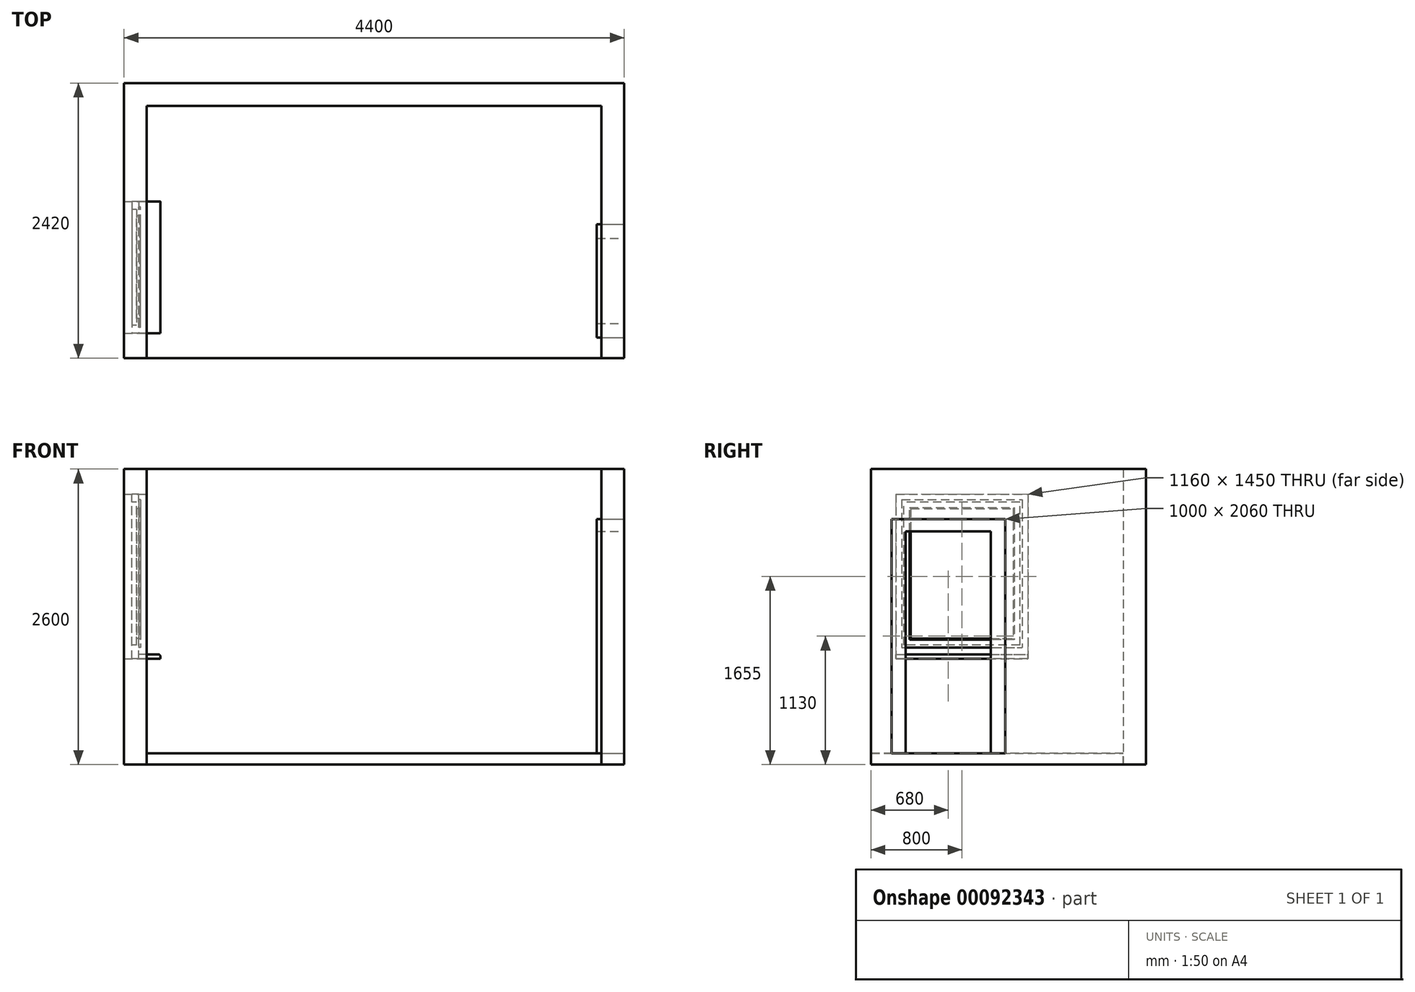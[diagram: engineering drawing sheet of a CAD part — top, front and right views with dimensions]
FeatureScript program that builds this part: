
annotation { "Feature Type Name" : "Feature", "Feature Type Description" : "" }
export const myFeature = defineFeature(function(context is Context, id is Id, definition is map)
    precondition{}
    {
        {
            var Q0;
            Q0=qCreatedBy(makeId("Top.planeOp"),FACE);
            var sketch = newSketch(context, id + "F0", { "sketchPlane" : qUnion([Q0])});
            skLineSegment(sketch, "E0", {"start": v(-2000, 1110) * mm, "end": v(2000, 1110) * mm});
            skLineSegment(sketch, "E1", {"start": v(2000, 1110) * mm, "end": v(2000, -1110) * mm});
            skLineSegment(sketch, "E2", {"start": v(2000, -1110) * mm, "end": v(-2000, -1110) * mm});
            skLineSegment(sketch, "E3", {"start": v(-2000, -1110) * mm, "end": v(-2000, 1110) * mm});
            skSolve(sketch);
        }
        {
            var Q0;
            Q0 = qSketchRegion(id + "F0", true);
            extrude(context, id + "F1", {"entities" : qUnion([Q0]), "oppositeDirection" : true, "depth" : 100 * mm});
        }
        {
            var Q0;
            Q0=makeQuery(id+"F1.opExtrude","CAP_FACE",FACE,{"disambiguationData":[OSD([sQuery(id+"F0.wireOp",EDGE,"E0"),sQuery(id+"F0.wireOp",EDGE,"E1"),sQuery(id+"F0.wireOp",EDGE,"E2"),sQuery(id+"F0.wireOp",EDGE,"E3")])],"isStart":true});
            var sketch = newSketch(context, id + "F2", { "sketchPlane" : qUnion([Q0])});
            skLineSegment(sketch, "E4", {"start": v(-2000, -1110) * mm, "end": v(-2000, 1110) * mm});
            skLineSegment(sketch, "E5", {"start": v(-2000, 1110) * mm, "end": v(2000, 1110) * mm});
            skLineSegment(sketch, "E6", {"start": v(2000, 1110) * mm, "end": v(2000, -1110) * mm});
            skLineSegment(sketch, "E7", {"start": v(2000, -1110) * mm, "end": v(2200, -1110) * mm});
            skLineSegment(sketch, "E8", {"start": v(2200, -1110) * mm, "end": v(2200, 1310) * mm});
            skLineSegment(sketch, "E9", {"start": v(2200, 1310) * mm, "end": v(-2200, 1310) * mm});
            skLineSegment(sketch, "E10", {"start": v(-2200, 1310) * mm, "end": v(-2200, -1110) * mm});
            skLineSegment(sketch, "E11", {"start": v(-2200, -1110) * mm, "end": v(-2000, -1110) * mm});
            skSolve(sketch);
        }
        {
            var Q0;
            Q0 = qSketchRegion(id + "F2", true);
            var Q1;
            Q1=makeQuery(id+"F1.opExtrude","CAP_FACE",FACE,{"disambiguationData":[OSD([sQuery(id+"F0.wireOp",EDGE,"E0"),sQuery(id+"F0.wireOp",EDGE,"E1"),sQuery(id+"F0.wireOp",EDGE,"E2"),sQuery(id+"F0.wireOp",EDGE,"E3")])],"isStart":false});
            extrude(context, id + "F3", {"entities" : qUnion([Q0]), "depth" : 2500 * mm, "hasSecondDirection" : true, "secondDirectionBound" : SecondDirectionBoundingType.UP_TO_SURFACE, "secondDirectionOppositeDirection" : true, "secondDirectionBoundEntityFace" : qUnion([Q1]), "secondDirectionDepth" : 25 * mm});
        }
        {
            var Q0;
            Q0=makeQuery(id+"F3.opExtrude","SWEPT_FACE",FACE,{"disambiguationData":[OSD([sQuery(id+"F2.wireOp",EDGE,"E4")])]});
            var sketch = newSketch(context, id + "F4", { "sketchPlane" : qUnion([Q0])});
            skLineSegment(sketch, "E12.bottom", {"start": v(-890, 2280) * mm, "end": v(270, 2280) * mm});
            skLineSegment(sketch, "E12.top", {"start": v(-890, 830) * mm, "end": v(270, 830) * mm});
            skLineSegment(sketch, "E12.left", {"start": v(-890, 2280) * mm, "end": v(-890, 830) * mm});
            skLineSegment(sketch, "E12.right", {"start": v(270, 2280) * mm, "end": v(270, 830) * mm});
            skSolve(sketch);
        }
        {
            var Q0;
            Q0 = qSketchRegion(id + "F4", true);
            extrude(context, id + "F5", {"entities" : qUnion([Q0]), "operationType" : NewBodyOperationType.REMOVE, "endBound" : BoundingType.UP_TO_NEXT, "oppositeDirection" : true, "depth" : 25 * mm});
        }
        {
            var Q0;
            Q0=makeQuery(id+"F3.opExtrude","SWEPT_FACE",FACE,{"disambiguationData":[OSD([sQuery(id+"F2.wireOp",EDGE,"E8")])]});
            var sketch = newSketch(context, id + "F6", { "sketchPlane" : qUnion([Q0])});
            skLineSegment(sketch, "E13.bottom", {"start": v(-930, 2060) * mm, "end": v(70, 2060) * mm});
            skLineSegment(sketch, "E13.top", {"start": v(-930, 0) * mm, "end": v(70, 0) * mm});
            skLineSegment(sketch, "E13.left", {"start": v(-930, 2060) * mm, "end": v(-930, 0) * mm});
            skLineSegment(sketch, "E13.right", {"start": v(70, 2060) * mm, "end": v(70, 0) * mm});
            skSolve(sketch);
        }
        {
            var Q0;
            Q0 = qSketchRegion(id + "F6", true);
            extrude(context, id + "F7", {"entities" : qUnion([Q0]), "operationType" : NewBodyOperationType.REMOVE, "endBound" : BoundingType.UP_TO_NEXT, "oppositeDirection" : true, "depth" : 25 * mm});
        }
        {
            var Q0;
            Q0=makeQuery(id+"F3.opExtrude","SWEPT_FACE",FACE,{"disambiguationData":[OSD([sQuery(id+"F2.wireOp",EDGE,"E8")])]});
            var sketch = newSketch(context, id + "F8", { "sketchPlane" : qUnion([Q0])});
            skLineSegment(sketch, "E14.bottom", {"start": v(-930, 2060) * mm, "end": v(70, 2060) * mm});
            skLineSegment(sketch, "E14.top", {"start": v(-930, 0) * mm, "end": v(-805, 0) * mm});
            skLineSegment(sketch, "E14.left", {"start": v(-930, 2060) * mm, "end": v(-930, 0) * mm});
            skLineSegment(sketch, "E14.right", {"start": v(70, 2060) * mm, "end": v(70, 0) * mm});
            skLineSegment(sketch, "E15.bottom", {"start": v(-805, 1950) * mm, "end": v(-55, 1950) * mm});
            skLineSegment(sketch, "E15.left", {"start": v(-805, 1950) * mm, "end": v(-805, 0) * mm});
            skLineSegment(sketch, "E15.right", {"start": v(-55, 1950) * mm, "end": v(-55, 0) * mm});
            skLineSegment(sketch, "E16.trimOffspring", {"start": v(-55, 0) * mm, "end": v(70, 0) * mm});
            skSolve(sketch);
        }
        {
            var Q0;
            Q0 = qSketchRegion(id + "F8", true);
            extrude(context, id + "F9", {"entities" : qUnion([Q0]), "oppositeDirection" : true, "depth" : 240 * mm});
        }
        {
            var Q0;
            Q0=makeQuery(id+"F3.opExtrude","SWEPT_FACE",FACE,{"disambiguationData":[OSD([sQuery(id+"F2.wireOp",EDGE,"E10")])]});
            var sketch = newSketch(context, id + "F10", { "sketchPlane" : qUnion([Q0])});
            skLineSegment(sketch, "E17.bottom", {"start": v(-270, 830) * mm, "end": v(890, 830) * mm});
            skLineSegment(sketch, "E17.top", {"start": v(-270, 2280) * mm, "end": v(890, 2280) * mm});
            skLineSegment(sketch, "E17.left", {"start": v(-270, 830) * mm, "end": v(-270, 2280) * mm});
            skLineSegment(sketch, "E17.right", {"start": v(890, 830) * mm, "end": v(890, 2280) * mm});
            skLineSegment(sketch, "E18.bottom", {"start": v(-200, 950) * mm, "end": v(820, 950) * mm});
            skLineSegment(sketch, "E18.top", {"start": v(-200, 2210) * mm, "end": v(820, 2210) * mm});
            skLineSegment(sketch, "E18.left", {"start": v(-200, 950) * mm, "end": v(-200, 2210) * mm});
            skLineSegment(sketch, "E18.right", {"start": v(820, 950) * mm, "end": v(820, 2210) * mm});
            skSolve(sketch);
        }
        {
            var Q0;
            Q0 = qSketchRegion(id + "F10", true);
            extrude(context, id + "F11", {"entities" : qUnion([Q0]), "oppositeDirection" : true, "depth" : 130 * mm, "hasSecondDirection" : true, "secondDirectionOppositeDirection" : true, "secondDirectionDepth" : 70 * mm});
        }
        {
            var Q0;
            Q0=makeQuery(id+"F11.opExtrude","CAP_FACE",FACE,{"disambiguationData":[OSD([sQuery(id+"F10.wireOp",EDGE,"E17.bottom"),sQuery(id+"F10.wireOp",EDGE,"E17.top"),sQuery(id+"F10.wireOp",EDGE,"E17.left"),sQuery(id+"F10.wireOp",EDGE,"E17.right"),sQuery(id+"F10.wireOp",EDGE,"E18.bottom"),sQuery(id+"F10.wireOp",EDGE,"E18.top"),sQuery(id+"F10.wireOp",EDGE,"E18.left"),sQuery(id+"F10.wireOp",EDGE,"E18.right")])],"isStart":false});
            var sketch = newSketch(context, id + "F12", { "sketchPlane" : qUnion([Q0])});
            skLineSegment(sketch, "E19.bottom", {"start": v(-840, 2230) * mm, "end": v(220, 2230) * mm});
            skLineSegment(sketch, "E19.top", {"start": v(-840, 930) * mm, "end": v(220, 930) * mm});
            skLineSegment(sketch, "E19.left", {"start": v(-840, 2230) * mm, "end": v(-840, 930) * mm});
            skLineSegment(sketch, "E19.right", {"start": v(220, 2230) * mm, "end": v(220, 930) * mm});
            skLineSegment(sketch, "E20.0", {"start": v(-760, 2150) * mm, "end": v(-760, 1010) * mm});
            skLineSegment(sketch, "E20.1", {"start": v(-760, 2150) * mm, "end": v(140, 2150) * mm});
            skLineSegment(sketch, "E20.2", {"start": v(140, 2150) * mm, "end": v(140, 1010) * mm});
            skLineSegment(sketch, "E20.3", {"start": v(-760, 1010) * mm, "end": v(140, 1010) * mm});
            skSolve(sketch);
        }
        {
            var Q0;
            Q0 = qSketchRegion(id + "F12", true);
            extrude(context, id + "F13", {"entities" : qUnion([Q0]), "operationType" : NewBodyOperationType.ADD, "depth" : 16 * mm, "hasSecondDirection" : true, "secondDirectionOppositeDirection" : true, "secondDirectionDepth" : 20 * mm});
        }
        {
            var Q0;
            Q0=makeQuery(id+"F13.opExtrude","CAP_EDGE",EDGE,{"disambiguationData":[OSD([sQuery(id+"F12.wireOp",EDGE,"E20.2")])],"isStart":false});
            var Q1;
            Q1=makeQuery(id+"F13.opExtrude","CAP_EDGE",EDGE,{"disambiguationData":[OSD([sQuery(id+"F12.wireOp",EDGE,"E20.3")])],"isStart":false});
            var Q2;
            Q2=makeQuery(id+"F13.opExtrude","CAP_EDGE",EDGE,{"disambiguationData":[OSD([sQuery(id+"F12.wireOp",EDGE,"E20.0")])],"isStart":false});
            var Q3;
            Q3=makeQuery(id+"F13.opExtrude","CAP_EDGE",EDGE,{"disambiguationData":[OSD([sQuery(id+"F12.wireOp",EDGE,"E20.1")])],"isStart":false});
            chamfer(context, id + "F14", {"entities" : qUnion([Q0, Q1, Q2, Q3]), "width" : 10 * mm, "tangentPropagation" : true});
        }
        {
            var Q0;
            Q0=makeQuery(id+"F11.opExtrude","CAP_FACE",FACE,{"disambiguationData":[OSD([sQuery(id+"F10.wireOp",EDGE,"E17.bottom"),sQuery(id+"F10.wireOp",EDGE,"E17.top"),sQuery(id+"F10.wireOp",EDGE,"E17.left"),sQuery(id+"F10.wireOp",EDGE,"E17.right"),sQuery(id+"F10.wireOp",EDGE,"E18.bottom"),sQuery(id+"F10.wireOp",EDGE,"E18.top"),sQuery(id+"F10.wireOp",EDGE,"E18.left"),sQuery(id+"F10.wireOp",EDGE,"E18.right")])],"isStart":false});
            var sketch = newSketch(context, id + "F15", { "sketchPlane" : qUnion([Q0])});
            skLineSegment(sketch, "E21.bottom", {"start": v(-890, 830) * mm, "end": v(270, 830) * mm});
            skLineSegment(sketch, "E21.top", {"start": v(-890, 870) * mm, "end": v(270, 870) * mm});
            skLineSegment(sketch, "E21.left", {"start": v(-890, 830) * mm, "end": v(-890, 870) * mm});
            skLineSegment(sketch, "E21.right", {"start": v(270, 830) * mm, "end": v(270, 870) * mm});
            skSolve(sketch);
        }
        {
            var Q0;
            Q0 = qSketchRegion(id + "F15", true);
            extrude(context, id + "F16", {"entities" : qUnion([Q0]), "depth" : 190 * mm});
        }
        {
            var Q0;
            Q0=makeQuery(id+"F16.opExtrude","CAP_EDGE",EDGE,{"disambiguationData":[OSD([sQuery(id+"F15.wireOp",EDGE,"E21.top")])],"isStart":false});
            fillet(context, id + "F17", {"entities" : qUnion([Q0]), "radius" : 20 * mm, "tangentPropagation" : true, "allowEdgeOverflow" : false});
        }
    });
